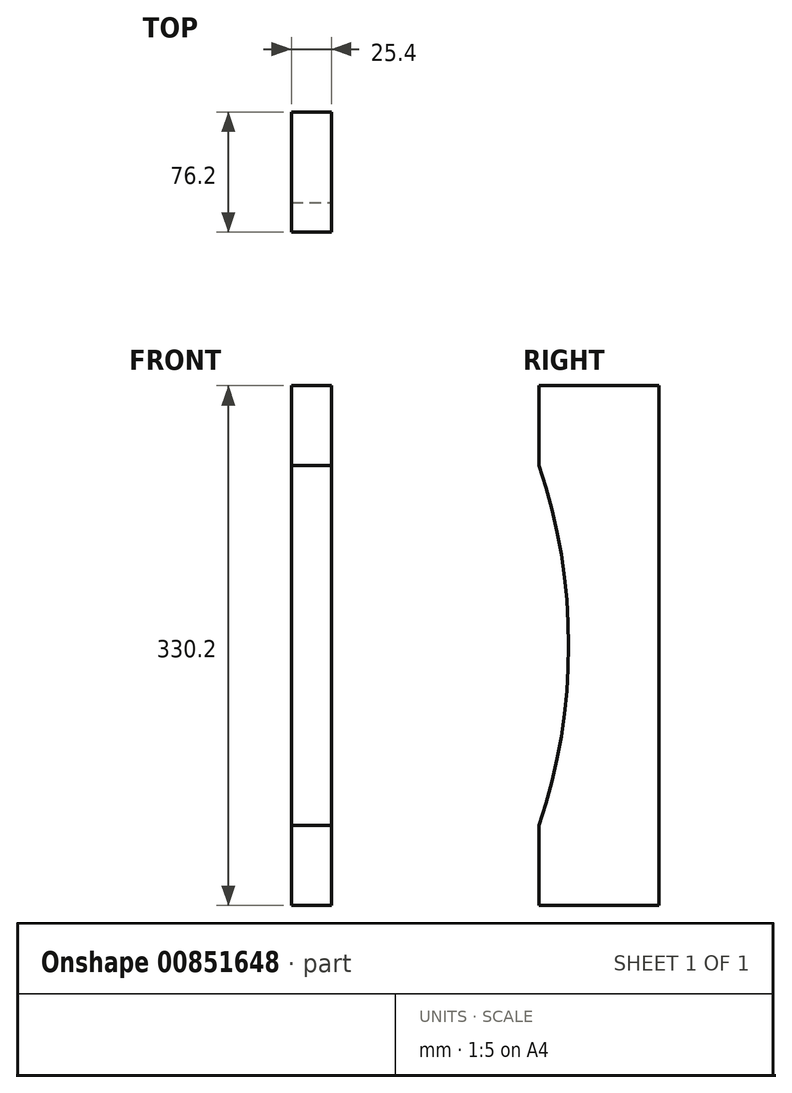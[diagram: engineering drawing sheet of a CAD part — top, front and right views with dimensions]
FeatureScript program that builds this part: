
annotation { "Feature Type Name" : "Feature", "Feature Type Description" : "" }
export const myFeature = defineFeature(function(context is Context, id is Id, definition is map)
    precondition{}
    {
        {
            var Q0;
            Q0=qCreatedBy(makeId("Front.planeOp"),FACE);
            var sketch = newSketch(context, id + "F0", { "sketchPlane" : qUnion([Q0])});
            skLineSegment(sketch, "E0", {"start": v(-25.4, 127.11) * mm, "end": v(-25.4, -203.09) * mm});
            skLineSegment(sketch, "E1", {"start": v(-25.4, 127.11) * mm, "end": v(0, 127.11) * mm});
            skLineSegment(sketch, "E2", {"start": v(0, 127.11) * mm, "end": v(0, -203.09) * mm});
            skLineSegment(sketch, "E3", {"start": v(0, -203.09) * mm, "end": v(-25.4, -203.09) * mm});
            skSolve(sketch);
        }
        {
            var Q0;
            Q0 = qSketchRegion(id + "F0", true);
            extrude(context, id + "F1", {"entities" : qUnion([Q0]), "depth" : 76.2 * mm, "offsetDistance" : 25.4 * mm});
        }
        {
            var Q0;
            Q0=makeQuery(id+"F1.opExtrude","SWEPT_FACE",FACE,{"disambiguationData":[OSD([sQuery(id+"F0.wireOp",EDGE,"E2")])]});
            var sketch = newSketch(context, id + "F2", { "sketchPlane" : qUnion([Q0])});
            skArc(sketch, "E4", {"start": v(-76.2, -152.29) * mm, "mid": v(-57.33, -37.99) * mm, "end": v(-76.2, 76.31) * mm});
            skSolve(sketch);
        }
        {
            var Q0;
            Q0 = qSketchRegion(id + "F2", true);
            var Q1;
            {var subQ0=sQuery(id+"F2.wireOp",EDGE,"E4");Q1=makeQuery(id+"F2.imprint","IMPRINT",FACE,{"disambiguationData":[TD([[makeQuery(id+"F2.imprint","IMPRINT",EDGE,{"derivedFrom":subQ0}),1.0]])]});}
            extrude(context, id + "F3", {"entities" : qUnion([Q0, Q1]), "operationType" : NewBodyOperationType.REMOVE, "oppositeDirection" : true, "depth" : 635 * mm, "offsetDistance" : 25.4 * mm});
        }
    });
